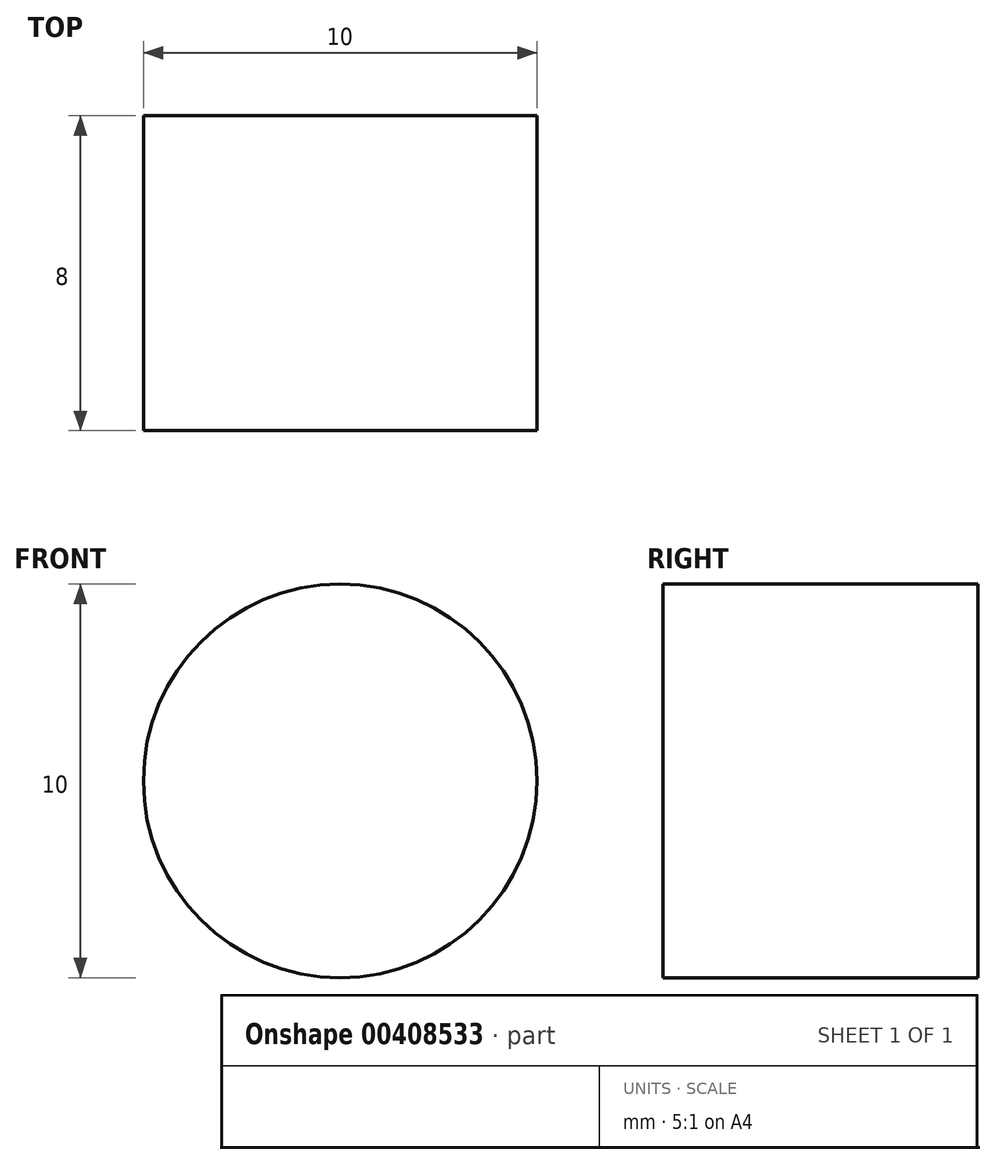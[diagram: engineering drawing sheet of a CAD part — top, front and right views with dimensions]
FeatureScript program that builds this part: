
annotation { "Feature Type Name" : "Feature", "Feature Type Description" : "" }
export const myFeature = defineFeature(function(context is Context, id is Id, definition is map)
    precondition{}
    {
        {
            var Q0;
            Q0=qCreatedBy(makeId("Front.planeOp"),FACE);
            var sketch = newSketch(context, id + "F0", { "sketchPlane" : qUnion([Q0])});
            skCircle(sketch, "E0", {"center": v(0, 0) * mm, "radius": 5 * mm});
            skSolve(sketch);
        }
        {
            var Q0;
            Q0 = qSketchRegion(id + "F0", true);
            extrude(context, id + "F1", {"entities" : qUnion([Q0]), "depth" : 8 * mm});
        }
    });
